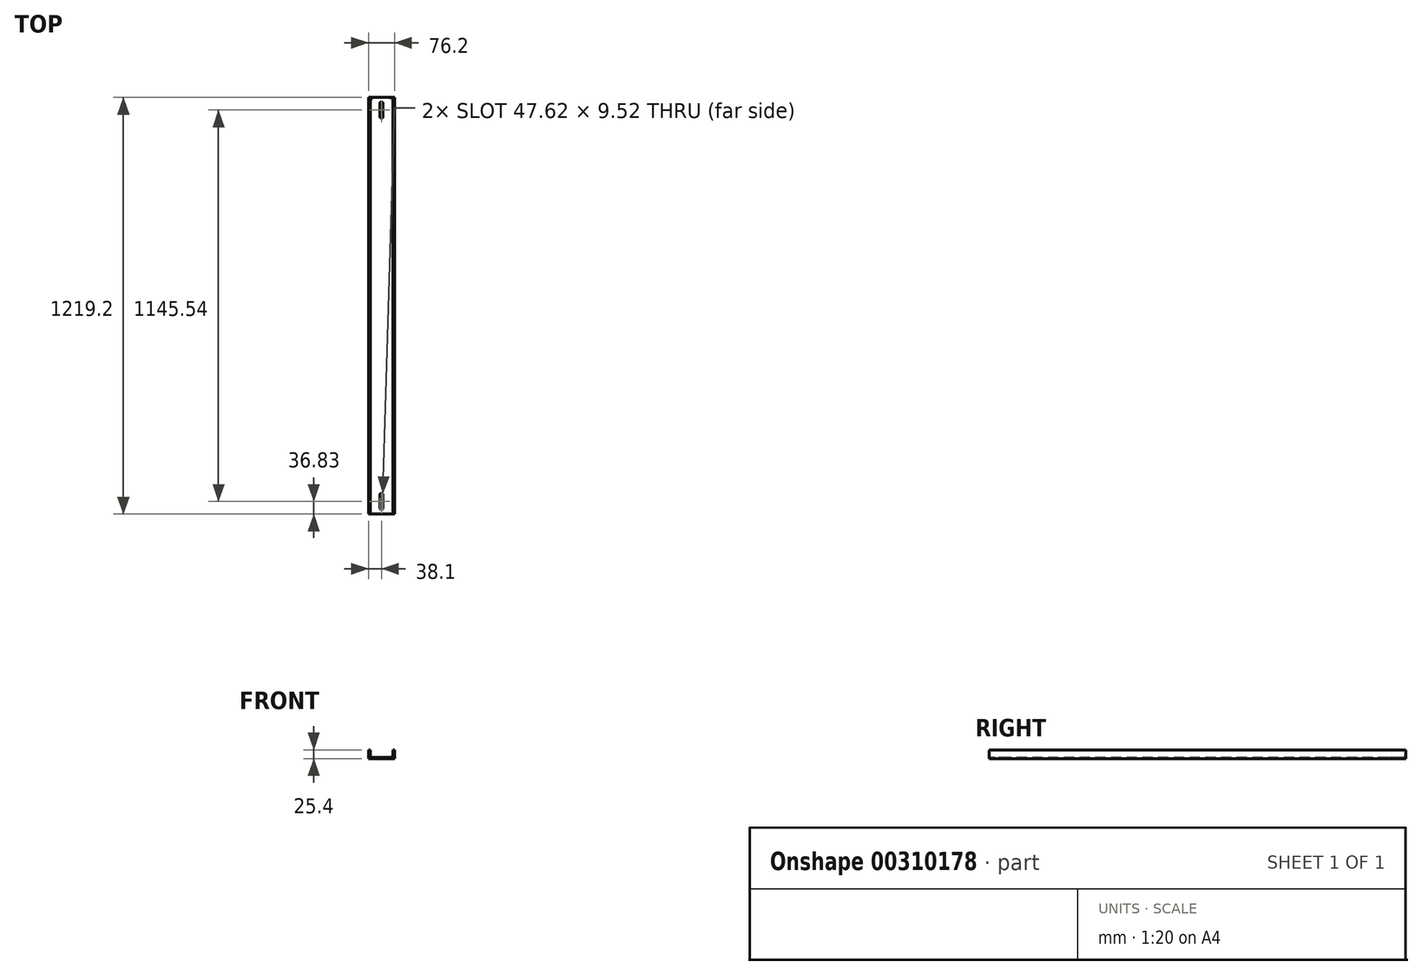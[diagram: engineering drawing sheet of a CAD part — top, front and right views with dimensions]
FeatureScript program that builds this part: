
annotation { "Feature Type Name" : "Feature", "Feature Type Description" : "" }
export const myFeature = defineFeature(function(context is Context, id is Id, definition is map)
    precondition{}
    {
        {
            var Q0;
            Q0=qCreatedBy(makeId("Front.planeOp"),FACE);
            var sketch = newSketch(context, id + "F0", { "sketchPlane" : qUnion([Q0])});
            skLineSegment(sketch, "E0.bottom", {"start": v(0, 0) * mm, "end": v(76.2, 0) * mm});
            skLineSegment(sketch, "E0.top", {"start": v(0, 25.4) * mm, "end": v(76.2, 25.4) * mm});
            skLineSegment(sketch, "E0.left", {"start": v(0, 0) * mm, "end": v(0, 25.4) * mm});
            skLineSegment(sketch, "E0.right", {"start": v(76.2, 0) * mm, "end": v(76.2, 25.4) * mm});
            skLineSegment(sketch, "E1.bottom", {"start": v(5.08, 25.4) * mm, "end": v(71.12, 25.4) * mm});
            skLineSegment(sketch, "E1.top", {"start": v(5.08, 3.81) * mm, "end": v(71.12, 3.81) * mm});
            skLineSegment(sketch, "E1.left", {"start": v(5.08, 25.4) * mm, "end": v(5.08, 3.81) * mm});
            skLineSegment(sketch, "E1.right", {"start": v(71.12, 25.4) * mm, "end": v(71.12, 3.8) * mm});
            skSolve(sketch);
        }
        {
            var Q0;
            Q0=makeQuery(id+"F0.imprint","IMPRINT",FACE,{"disambiguationData":[TD([[makeQuery(id+"F0.imprint","IMPRINT",EDGE,{"derivedFrom":sQuery(id+"F0.wireOp",EDGE,"E0.bottom")}),1.0]])]});
            extrude(context, id + "F1", {"entities" : qUnion([Q0]), "oppositeDirection" : true, "depth" : 1219.2 * mm});
        }
        {
            var Q0;
            Q0=makeQuery(id+"F1.opExtrude","SWEPT_FACE",FACE,{"disambiguationData":[OSD([sQuery(id+"F0.wireOp",EDGE,"E1.top")])]});
            var sketch = newSketch(context, id + "F2", { "sketchPlane" : qUnion([Q0])});
            skPoint(sketch, "E2.positionSnap0", {"position": v(38.1, 0) * mm});
            skPoint(sketch, "E3", {"position": v(38.1, 17.78) * mm});
            skPoint(sketch, "E4", {"position": v(38.1, 55.88) * mm});
            skArc(sketch, "E5", {"start": v(33.34, 17.78) * mm, "mid": v(38.1, 13.02) * mm, "end": v(42.86, 17.78) * mm});
            skArc(sketch, "E6", {"start": v(42.86, 55.88) * mm, "mid": v(38.1, 60.64) * mm, "end": v(33.34, 55.88) * mm});
            skLineSegment(sketch, "E7", {"start": v(33.34, 55.88) * mm, "end": v(33.34, 17.78) * mm});
            skLineSegment(sketch, "E8", {"start": v(42.86, 17.78) * mm, "end": v(42.86, 55.88) * mm});
            skSolve(sketch);
        }
        {
            var Q0;
            Q0=makeQuery(id+"F2.imprint","IMPRINT",FACE,{"disambiguationData":[TD([[makeQuery(id+"F2.imprint","IMPRINT",EDGE,{"derivedFrom":sQuery(id+"F2.wireOp",EDGE,"E5")}),1.0]])]});
            extrude(context, id + "F3", {"entities" : qUnion([Q0]), "operationType" : NewBodyOperationType.REMOVE, "oppositeDirection" : true, "depth" : 25.4 * mm});
        }
        {
            var Q0;
            Q0=makeQuery(id+"F1.opExtrude","SWEPT_FACE",FACE,{"disambiguationData":[OSD([sQuery(id+"F0.wireOp",EDGE,"E1.top")])]});
            var sketch = newSketch(context, id + "F4", { "sketchPlane" : qUnion([Q0])});
            skPoint(sketch, "E9", {"position": v(38.1, 1201.42) * mm});
            skPoint(sketch, "E9.positionSnap0", {"position": v(38.1, 1219.2) * mm});
            skPoint(sketch, "E10", {"position": v(38.1, 1163.32) * mm});
            skArc(sketch, "E11", {"start": v(42.86, 1201.42) * mm, "mid": v(38.1, 1206.18) * mm, "end": v(33.34, 1201.42) * mm});
            skArc(sketch, "E12", {"start": v(33.34, 1163.32) * mm, "mid": v(38.32, 1158.56) * mm, "end": v(42.84, 1163.75) * mm});
            skLineSegment(sketch, "E13", {"start": v(33.34, 1201.42) * mm, "end": v(33.34, 1163.32) * mm});
            skLineSegment(sketch, "E14", {"start": v(42.84, 1162.88) * mm, "end": v(42.86, 1201.42) * mm});
            skSolve(sketch);
        }
        {
            var Q0;
            {var subQ5=sQuery(id+"F4.wireOp",EDGE,"E11");Q0=makeQuery(id+"F4.imprint","IMPRINT",FACE,{"disambiguationData":[TD([[makeQuery(id+"F4.imprint","IMPRINT",EDGE,{"derivedFrom":subQ5}),1.0]])]});}
            extrude(context, id + "F5", {"entities" : qUnion([Q0]), "operationType" : NewBodyOperationType.REMOVE, "oppositeDirection" : true, "depth" : 25.4 * mm});
        }
        {
            var Q0;
            Q0=makeQuery(id+"F1.opExtrude","CAP_EDGE",EDGE,{"disambiguationData":[OSD([sQuery(id+"F0.wireOp",EDGE,"E1.top")])],"isStart":false});
            var Q1;
            Q1=makeQuery(id+"F1.opExtrude","CAP_EDGE",EDGE,{"disambiguationData":[OSD([sQuery(id+"F0.wireOp",EDGE,"E1.left")])],"isStart":false});
            var Q2;
            Q2=makeQuery(id+"F1.opExtrude","CAP_EDGE",EDGE,{"disambiguationData":[OSD([sQuery(id+"F0.wireOp",EDGE,"E1.right")])],"isStart":false});
            fillet(context, id + "F6", {"entities" : qUnion([Q0, Q1, Q2]), "radius" : 5.08 * mm, "tangentPropagation" : true, "allowEdgeOverflow" : false});
        }
        {
            var Q0;
            Q0=makeQuery(id+"F1.opExtrude","SWEPT_EDGE",EDGE,{"disambiguationData":[OSD([sQuery(id+"F0.wireOp",EDGE,"E1.top"),sQuery(id+"F0.wireOp",EDGE,"E1.left")])]});
            fillet(context, id + "F7", {"entities" : qUnion([Q0]), "radius" : 5.08 * mm, "tangentPropagation" : true, "allowEdgeOverflow" : false});
        }
        {
            var Q0;
            Q0=makeQuery(id+"F1.opExtrude","SWEPT_EDGE",EDGE,{"disambiguationData":[OSD([sQuery(id+"F0.wireOp",EDGE,"E1.top"),sQuery(id+"F0.wireOp",EDGE,"E1.right")])]});
            fillet(context, id + "F8", {"entities" : qUnion([Q0]), "radius" : 5.08 * mm, "tangentPropagation" : true, "allowEdgeOverflow" : false});
        }
    });
